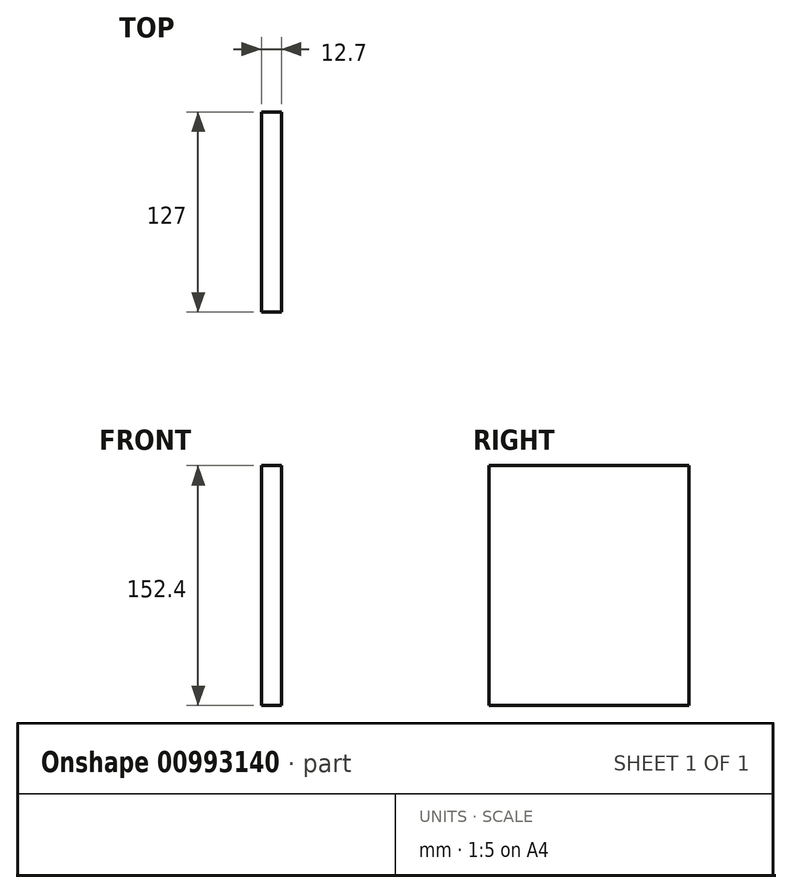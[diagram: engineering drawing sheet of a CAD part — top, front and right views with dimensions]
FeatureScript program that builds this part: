
annotation { "Feature Type Name" : "Feature", "Feature Type Description" : "" }
export const myFeature = defineFeature(function(context is Context, id is Id, definition is map)
    precondition{}
    {
        {
            var Q0;
            Q0=qCreatedBy(makeId("Right.planeOp"),FACE);
            var sketch = newSketch(context, id + "F0", { "sketchPlane" : qUnion([Q0])});
            skLineSegment(sketch, "E0.bottom", {"start": v(-119.6, 96.44) * mm, "end": v(7.4, 96.44) * mm});
            skLineSegment(sketch, "E0.top", {"start": v(-119.6, -55.96) * mm, "end": v(7.4, -55.96) * mm});
            skLineSegment(sketch, "E0.left", {"start": v(-119.6, 96.44) * mm, "end": v(-119.6, -55.96) * mm});
            skLineSegment(sketch, "E0.right", {"start": v(7.4, 96.44) * mm, "end": v(7.4, -55.96) * mm});
            skSolve(sketch);
        }
        {
            var Q0;
            Q0=makeQuery(id+"F0.imprint","IMPRINT",FACE,{"disambiguationData":[TD([[makeQuery(id+"F0.imprint","IMPRINT",EDGE,{"derivedFrom":sQuery(id+"F0.wireOp",EDGE,"E0.bottom")}),-1.0]])]});
            extrude(context, id + "F1", {"entities" : qUnion([Q0]), "depth" : 12.7 * mm, "offsetDistance" : 25.4 * mm});
        }
    });
